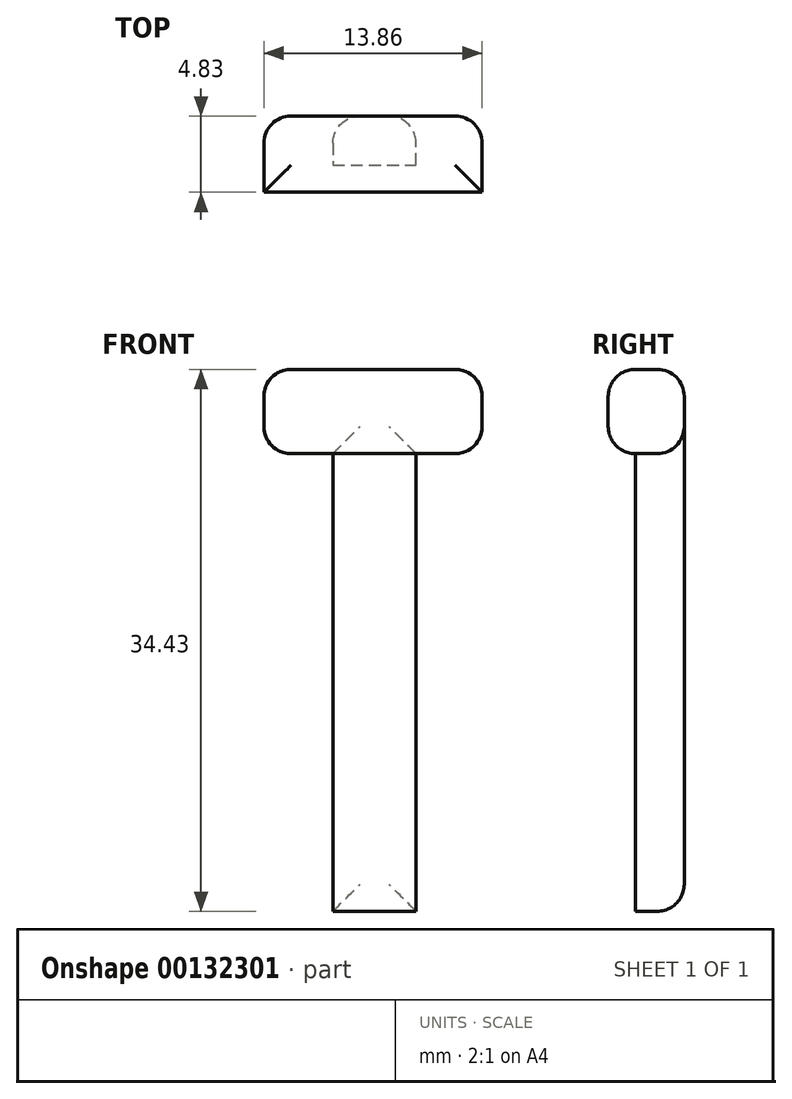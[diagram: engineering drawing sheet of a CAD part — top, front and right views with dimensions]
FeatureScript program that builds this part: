
annotation { "Feature Type Name" : "Feature", "Feature Type Description" : "" }
export const myFeature = defineFeature(function(context is Context, id is Id, definition is map)
    precondition{}
    {
        {
            var Q0;
            Q0=qCreatedBy(makeId("Front.planeOp"),FACE);
            var sketch = newSketch(context, id + "F0", { "sketchPlane" : qUnion([Q0])});
            skLineSegment(sketch, "E0", {"start": v(-12.34, 0) * mm, "end": v(-12.34, 29.09) * mm});
            skLineSegment(sketch, "E1", {"start": v(-7.05, 0) * mm, "end": v(-7.05, 29.09) * mm});
            skLineSegment(sketch, "E2", {"start": v(-7.05, 29.09) * mm, "end": v(-12.34, 29.09) * mm});
            skLineSegment(sketch, "E3", {"start": v(-12.34, 0) * mm, "end": v(-7.05, 0) * mm});
            skSolve(sketch);
        }
        {
            var Q0;
            Q0 = qSketchRegion(id + "F0", true);
            extrude(context, id + "F1", {"entities" : qUnion([Q0]), "depth" : 3.1 * mm});
        }
        {
            var Q0;
            Q0=qCreatedBy(makeId("Front.planeOp"),FACE);
            var sketch = newSketch(context, id + "F2", { "sketchPlane" : qUnion([Q0])});
            skLineSegment(sketch, "E4", {"start": v(-12.29, 29.07) * mm, "end": v(-16.71, 29.07) * mm});
            skLineSegment(sketch, "E5", {"start": v(-16.71, 29.07) * mm, "end": v(-16.71, 34.43) * mm});
            skLineSegment(sketch, "E6", {"start": v(-16.71, 34.43) * mm, "end": v(-2.85, 34.43) * mm});
            skLineSegment(sketch, "E7", {"start": v(-2.85, 34.43) * mm, "end": v(-2.85, 29.07) * mm});
            skLineSegment(sketch, "E8", {"start": v(-2.85, 29.07) * mm, "end": v(-7.05, 29.07) * mm});
            skLineSegment(sketch, "E9", {"start": v(-12.29, 29.07) * mm, "end": v(-7.05, 29.07) * mm});
            skSolve(sketch);
        }
        {
            var Q0;
            Q0 = qSketchRegion(id + "F2", true);
            extrude(context, id + "F3", {"entities" : qUnion([Q0]), "operationType" : NewBodyOperationType.ADD, "depth" : 4.83 * mm});
        }
        {
            var Q0;
            Q0=makeQuery(id+"F3.opExtrude","SWEPT_EDGE",EDGE,{"disambiguationData":[OSD([sQuery(id+"F2.wireOp",EDGE,"E5"),sQuery(id+"F2.wireOp",EDGE,"E6")])]});
            var Q1;
            Q1=makeQuery(id+"F3.opExtrude","SWEPT_EDGE",EDGE,{"disambiguationData":[OSD([sQuery(id+"F2.wireOp",EDGE,"E4"),sQuery(id+"F2.wireOp",EDGE,"E5")])]});
            var Q2;
            Q2=makeQuery(id+"F3.opExtrude","SWEPT_EDGE",EDGE,{"disambiguationData":[OSD([sQuery(id+"F2.wireOp",EDGE,"E6"),sQuery(id+"F2.wireOp",EDGE,"E7")])]});
            var Q3;
            Q3=makeQuery(id+"F3.opExtrude","CAP_EDGE",EDGE,{"disambiguationData":[OSD([sQuery(id+"F2.wireOp",EDGE,"E4"),sQuery(id+"F2.wireOp",EDGE,"E8"),sQuery(id+"F2.wireOp",EDGE,"E9")])],"isStart":false});
            var Q4;
            Q4=makeQuery(id+"F3.opExtrude","SWEPT_EDGE",EDGE,{"disambiguationData":[OSD([sQuery(id+"F2.wireOp",EDGE,"E7"),sQuery(id+"F2.wireOp",EDGE,"E8")])]});
            var Q5;
            Q5=makeQuery(id+"F3.opExtrude","CAP_EDGE",EDGE,{"disambiguationData":[OSD([sQuery(id+"F2.wireOp",EDGE,"E6")])],"isStart":false});
            var Q6;
            Q6=makeQuery(id+"F3.boolean.opBoolean","MERGE",FACE,{"derivedFrom":[makeQuery(id+"F1.opExtrude","CAP_FACE",FACE,{"disambiguationData":[OSD([sQuery(id+"F0.wireOp",EDGE,"E0"),sQuery(id+"F0.wireOp",EDGE,"E1"),sQuery(id+"F0.wireOp",EDGE,"E2"),sQuery(id+"F0.wireOp",EDGE,"E3")])],"isStart":true}),makeQuery(id+"F3.opExtrude","CAP_FACE",FACE,{"disambiguationData":[OSD([sQuery(id+"F2.wireOp",EDGE,"E4"),sQuery(id+"F2.wireOp",EDGE,"E5"),sQuery(id+"F2.wireOp",EDGE,"E6"),sQuery(id+"F2.wireOp",EDGE,"E7"),sQuery(id+"F2.wireOp",EDGE,"E8"),sQuery(id+"F2.wireOp",EDGE,"E9")])],"isStart":true})]});
            fillet(context, id + "F4", {"entities" : qUnion([Q0, Q1, Q2, Q3, Q4, Q5, Q6]), "radius" : 1.71 * mm, "tangentPropagation" : true, "allowEdgeOverflow" : false});
        }
    });
